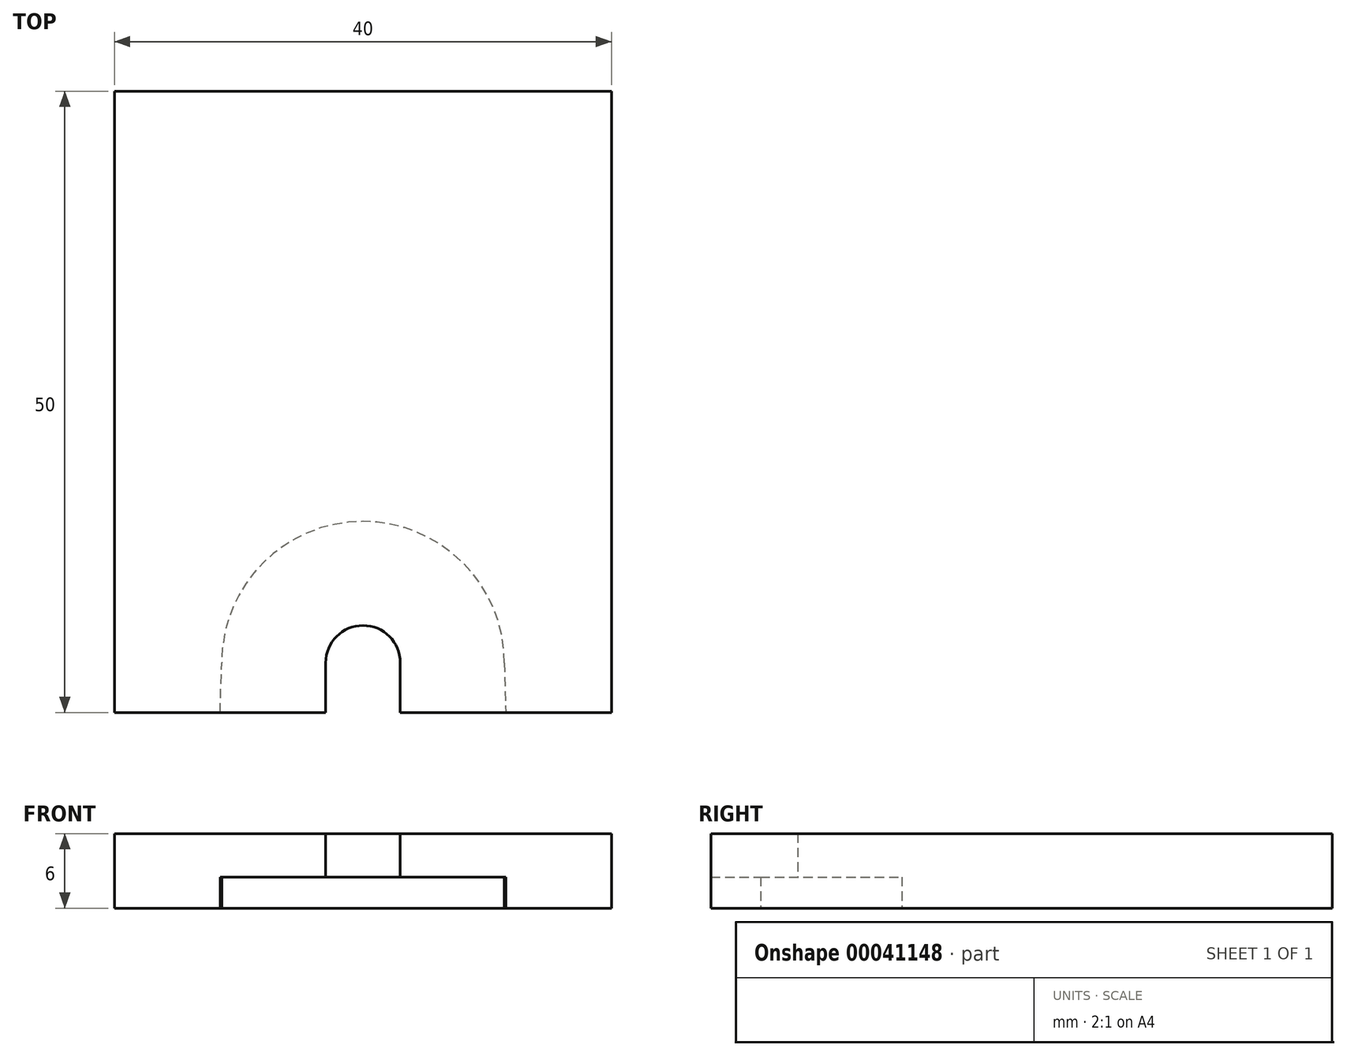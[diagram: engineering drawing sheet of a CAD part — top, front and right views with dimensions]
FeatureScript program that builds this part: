
annotation { "Feature Type Name" : "Feature", "Feature Type Description" : "" }
export const myFeature = defineFeature(function(context is Context, id is Id, definition is map)
    precondition{}
    {
        {
            var Q0;
            Q0=qCreatedBy(makeId("Top.planeOp"),FACE);
            var sketch = newSketch(context, id + "F0", { "sketchPlane" : qUnion([Q0])});
            skLineSegment(sketch, "E0.bottom", {"start": v(0, 24.28) * mm, "end": v(-40, 24.28) * mm});
            skLineSegment(sketch, "E0.top", {"start": v(0, -25.72) * mm, "end": v(-40, -25.72) * mm});
            skLineSegment(sketch, "E0.left", {"start": v(0, 24.28) * mm, "end": v(0, -25.72) * mm});
            skLineSegment(sketch, "E0.right", {"start": v(-40, 24.28) * mm, "end": v(-40, -25.72) * mm});
            skCircle(sketch, "E1", {"center": v(-20, -21.72) * mm, "radius": 3 * mm});
            skPoint(sketch, "E1.centerSnap0", {"position": v(-20, -25.72) * mm});
            skLineSegment(sketch, "E2", {"start": v(-17, -21.72) * mm, "end": v(-17, -25.72) * mm});
            skLineSegment(sketch, "E3", {"start": v(-23, -21.72) * mm, "end": v(-23, -25.72) * mm});
            skSolve(sketch);
        }
        {
            var Q0;
            Q0=makeQuery(id+"F0.imprint","IMPRINT",FACE,{"disambiguationData":[TD([[makeQuery(id+"F0.imprint","IMPRINT",EDGE,{"derivedFrom":sQuery(id+"F0.wireOp",EDGE,"E0.bottom")}),1.0]])]});
            extrude(context, id + "F1", {"entities" : qUnion([Q0]), "depth" : 6 * mm});
        }
        {
            var Q0;
            Q0=makeQuery(id+"F1.opExtrude","CAP_FACE",FACE,{"disambiguationData":[OSD([sQuery(id+"F0.wireOp",EDGE,"E0.bottom"),sQuery(id+"F0.wireOp",EDGE,"E0.top"),sQuery(id+"F0.wireOp",EDGE,"E0.left"),sQuery(id+"F0.wireOp",EDGE,"E0.right")])],"isStart":true});
            var sketch = newSketch(context, id + "F2", { "sketchPlane" : qUnion([Q0])});
            skPoint(sketch, "E4.centerSnap0", {"position": v(-8.5, 25.72) * mm});
            skCircle(sketch, "E5", {"center": v(-20, 21.72) * mm, "radius": 11.37 * mm});
            skLineSegment(sketch, "E6", {"start": v(-8.63, 21.72) * mm, "end": v(-8.5, 25.72) * mm});
            skLineSegment(sketch, "E7", {"start": v(-30.64, 25.72) * mm, "end": v(-8.5, 25.72) * mm});
            skLineSegment(sketch, "E8", {"start": v(-30.64, 25.72) * mm, "end": v(-31.5, 25.72) * mm});
            skLineSegment(sketch, "E9", {"start": v(-31.5, 25.72) * mm, "end": v(-31.37, 21.72) * mm});
            skSolve(sketch);
        }
        {
            var Q0;
            Q0 = qSketchRegion(id + "F2", true);
            extrude(context, id + "F3", {"entities" : qUnion([Q0]), "operationType" : NewBodyOperationType.REMOVE, "oppositeDirection" : true, "depth" : 2.5 * mm});
        }
    });
